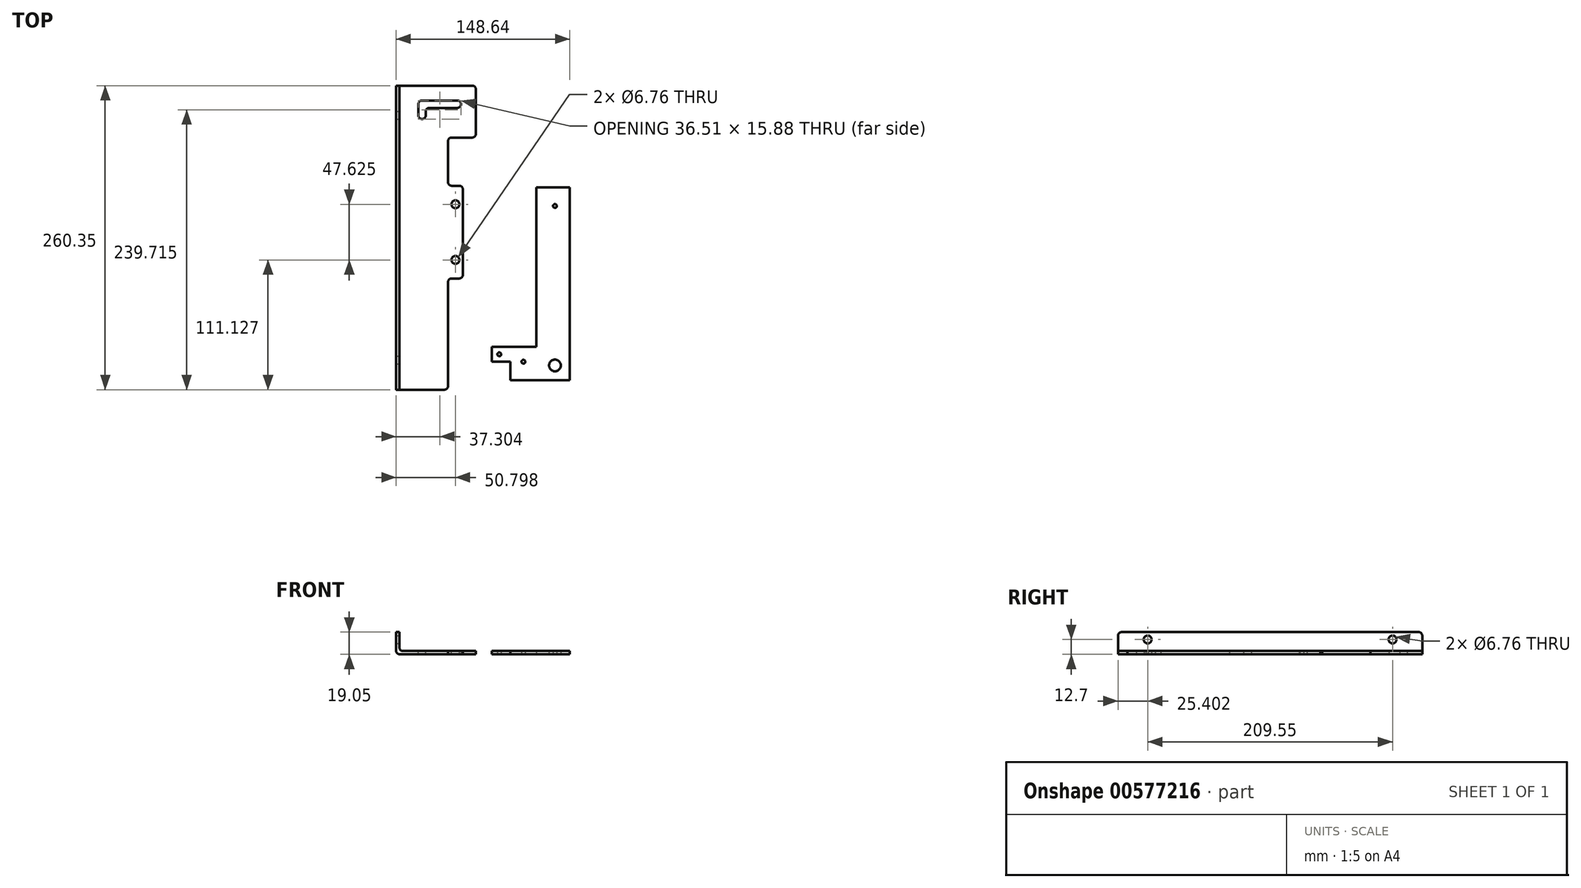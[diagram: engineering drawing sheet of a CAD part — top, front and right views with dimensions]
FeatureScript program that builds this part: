
annotation { "Feature Type Name" : "Feature", "Feature Type Description" : "" }
export const myFeature = defineFeature(function(context is Context, id is Id, definition is map)
    precondition{}
    {
        {
            var Q0;
            Q0=qCreatedBy(makeId("Top.planeOp"),FACE);
            var sketch = newSketch(context, id + "F0", { "sketchPlane" : qUnion([Q0])});
            skLineSegment(sketch, "E0", {"start": v(-43.32, 198.66) * mm, "end": v(-43.32, -61.69) * mm});
            skLineSegment(sketch, "E1", {"start": v(-43.32, -61.69) * mm, "end": v(1.13, -61.69) * mm});
            skLineSegment(sketch, "E2", {"start": v(1.13, -61.69) * mm, "end": v(1.13, 33.56) * mm});
            skLineSegment(sketch, "E3", {"start": v(1.13, 33.56) * mm, "end": v(13.83, 33.56) * mm});
            skLineSegment(sketch, "E4", {"start": v(13.83, 33.56) * mm, "end": v(13.83, 112.94) * mm});
            skLineSegment(sketch, "E5", {"start": v(13.83, 112.94) * mm, "end": v(1.13, 112.94) * mm});
            skLineSegment(sketch, "E6", {"start": v(1.13, 112.94) * mm, "end": v(1.13, 154.21) * mm});
            skLineSegment(sketch, "E7", {"start": v(1.13, 154.21) * mm, "end": v(24.94, 154.21) * mm});
            skLineSegment(sketch, "E8", {"start": v(24.94, 154.21) * mm, "end": v(24.94, 198.66) * mm});
            skLineSegment(sketch, "E9", {"start": v(-43.32, 198.66) * mm, "end": v(24.94, 198.66) * mm});
            skLineSegment(sketch, "E10", {"start": v(105.32, 111.48) * mm, "end": v(76.75, 111.48) * mm});
            skLineSegment(sketch, "E11", {"start": v(76.75, 111.48) * mm, "end": v(76.75, -25.05) * mm});
            skLineSegment(sketch, "E12", {"start": v(76.75, -25.05) * mm, "end": v(38.65, -25.05) * mm});
            skLineSegment(sketch, "E13", {"start": v(38.65, -25.05) * mm, "end": v(38.65, -37.75) * mm});
            skLineSegment(sketch, "E14", {"start": v(38.65, -37.75) * mm, "end": v(54.52, -37.75) * mm});
            skLineSegment(sketch, "E15", {"start": v(54.52, -37.75) * mm, "end": v(54.52, -53.62) * mm});
            skLineSegment(sketch, "E16", {"start": v(54.52, -53.62) * mm, "end": v(105.32, -53.62) * mm});
            skLineSegment(sketch, "E17", {"start": v(105.32, -53.62) * mm, "end": v(105.32, 111.48) * mm});
            skSolve(sketch);
        }
        {
            var Q0;
            Q0=makeQuery(id+"F0.imprint","IMPRINT",FACE,{"disambiguationData":[TD([[makeQuery(id+"F0.imprint","IMPRINT",EDGE,{"derivedFrom":sQuery(id+"F0.wireOp",EDGE,"E0")}),1.0]])]});
            extrude(context, id + "F1", {"entities" : qUnion([Q0]), "depth" : 19.05 * mm, "offsetDistance" : 25.4 * mm});
        }
        {
            var Q0;
            Q0=makeQuery(id+"F0.imprint","IMPRINT",FACE,{"disambiguationData":[TD([[makeQuery(id+"F0.imprint","IMPRINT",EDGE,{"derivedFrom":sQuery(id+"F0.wireOp",EDGE,"E10")}),1.0]])]});
            extrude(context, id + "F2", {"entities" : qUnion([Q0]), "depth" : 2.78 * mm, "offsetDistance" : 25.4 * mm});
        }
        {
            var Q0;
            Q0=makeQuery(id+"F1.opExtrude","CAP_FACE",FACE,{"disambiguationData":[OSD([sQuery(id+"F0.wireOp",EDGE,"E0"),sQuery(id+"F0.wireOp",EDGE,"E1"),sQuery(id+"F0.wireOp",EDGE,"E2"),sQuery(id+"F0.wireOp",EDGE,"E3"),sQuery(id+"F0.wireOp",EDGE,"E4"),sQuery(id+"F0.wireOp",EDGE,"E5"),sQuery(id+"F0.wireOp",EDGE,"E6"),sQuery(id+"F0.wireOp",EDGE,"E7"),sQuery(id+"F0.wireOp",EDGE,"E8"),sQuery(id+"F0.wireOp",EDGE,"E9")])],"isStart":false});
            var Q1;
            Q1=makeQuery(id+"F1.opExtrude","SWEPT_FACE",FACE,{"disambiguationData":[OSD([sQuery(id+"F0.wireOp",EDGE,"E4")])]});
            var Q2;
            Q2=makeQuery(id+"F1.opExtrude","SWEPT_FACE",FACE,{"disambiguationData":[OSD([sQuery(id+"F0.wireOp",EDGE,"E8")])]});
            var Q3;
            Q3=makeQuery(id+"F1.opExtrude","SWEPT_FACE",FACE,{"disambiguationData":[OSD([sQuery(id+"F0.wireOp",EDGE,"E1")])]});
            var Q4;
            Q4=makeQuery(id+"F1.opExtrude","SWEPT_FACE",FACE,{"disambiguationData":[OSD([sQuery(id+"F0.wireOp",EDGE,"E2")])]});
            var Q5;
            Q5=makeQuery(id+"F1.opExtrude","SWEPT_FACE",FACE,{"disambiguationData":[OSD([sQuery(id+"F0.wireOp",EDGE,"E3")])]});
            var Q6;
            Q6=makeQuery(id+"F1.opExtrude","SWEPT_FACE",FACE,{"disambiguationData":[OSD([sQuery(id+"F0.wireOp",EDGE,"E5")])]});
            var Q7;
            Q7=makeQuery(id+"F1.opExtrude","SWEPT_FACE",FACE,{"disambiguationData":[OSD([sQuery(id+"F0.wireOp",EDGE,"E6")])]});
            var Q8;
            Q8=makeQuery(id+"F1.opExtrude","SWEPT_FACE",FACE,{"disambiguationData":[OSD([sQuery(id+"F0.wireOp",EDGE,"E7")])]});
            var Q9;
            Q9=makeQuery(id+"F1.opExtrude","SWEPT_FACE",FACE,{"disambiguationData":[OSD([sQuery(id+"F0.wireOp",EDGE,"E9")])]});
            shell(context, id + "F3", {"entities" : qUnion([Q0, Q1, Q2, Q3, Q4, Q5, Q6, Q7, Q8, Q9]), "thickness" : 2.78 * mm});
        }
        {
            var Q0;
            Q0=makeQuery(id+"F3.opShell","OFFSET_FACE",FACE,{"disambiguationData":[OSD([sQuery(id+"F0.wireOp",EDGE,"E0"),sQuery(id+"F0.wireOp",EDGE,"E1"),sQuery(id+"F0.wireOp",EDGE,"E2"),sQuery(id+"F0.wireOp",EDGE,"E3"),sQuery(id+"F0.wireOp",EDGE,"E4"),sQuery(id+"F0.wireOp",EDGE,"E5"),sQuery(id+"F0.wireOp",EDGE,"E6"),sQuery(id+"F0.wireOp",EDGE,"E7"),sQuery(id+"F0.wireOp",EDGE,"E8"),sQuery(id+"F0.wireOp",EDGE,"E9")])]});
            var sketch = newSketch(context, id + "F4", { "sketchPlane" : qUnion([Q0])});
            skLineSegment(sketch, "E18", {"start": v(12.24, 185.96) * mm, "end": v(-24.27, 185.96) * mm});
            skLineSegment(sketch, "E19", {"start": v(-24.27, 185.96) * mm, "end": v(-24.27, 170.09) * mm});
            skLineSegment(sketch, "E20", {"start": v(-24.27, 170.09) * mm, "end": v(-17.92, 170.09) * mm});
            skLineSegment(sketch, "E21", {"start": v(-17.92, 170.09) * mm, "end": v(-17.92, 179.61) * mm});
            skLineSegment(sketch, "E22", {"start": v(-17.92, 179.61) * mm, "end": v(12.24, 179.61) * mm});
            skLineSegment(sketch, "E23", {"start": v(12.24, 179.61) * mm, "end": v(12.24, 185.96) * mm});
            skSolve(sketch);
        }
        {
            var Q0;
            Q0 = qSketchRegion(id + "F4", true);
            extrude(context, id + "F5", {"entities" : qUnion([Q0]), "operationType" : NewBodyOperationType.REMOVE, "oppositeDirection" : true, "depth" : 25.4 * mm, "offsetDistance" : 25.4 * mm});
        }
        {
            var Q0;
            Q0=makeQuery(id+"F3.opShell","OFFSET_FACE",FACE,{"disambiguationData":[OSD([sQuery(id+"F0.wireOp",EDGE,"E0"),sQuery(id+"F0.wireOp",EDGE,"E1"),sQuery(id+"F0.wireOp",EDGE,"E2"),sQuery(id+"F0.wireOp",EDGE,"E3"),sQuery(id+"F0.wireOp",EDGE,"E4"),sQuery(id+"F0.wireOp",EDGE,"E5"),sQuery(id+"F0.wireOp",EDGE,"E6"),sQuery(id+"F0.wireOp",EDGE,"E7"),sQuery(id+"F0.wireOp",EDGE,"E8"),sQuery(id+"F0.wireOp",EDGE,"E9")])]});
            var sketch = newSketch(context, id + "F6", { "sketchPlane" : qUnion([Q0])});
            skPoint(sketch, "E24", {"position": v(7.48, 97.06) * mm});
            skPoint(sketch, "E25", {"position": v(7.48, 49.44) * mm});
            skSolve(sketch);
        }
        {
            var Q0;
            Q0=sQuery(id+"F6.wireOp",VERTEX,"E24");
            var Q1;
            Q1=sQuery(id+"F6.wireOp",VERTEX,"E25");
            var Q2;
            Q2=makeQuery(id+"F1.opExtrude","SWEPT_BODY",BODY,{"disambiguationData":[OSD([sQuery(id+"F0.wireOp",EDGE,"E0"),sQuery(id+"F0.wireOp",EDGE,"E1"),sQuery(id+"F0.wireOp",EDGE,"E2"),sQuery(id+"F0.wireOp",EDGE,"E3"),sQuery(id+"F0.wireOp",EDGE,"E4"),sQuery(id+"F0.wireOp",EDGE,"E5"),sQuery(id+"F0.wireOp",EDGE,"E6"),sQuery(id+"F0.wireOp",EDGE,"E7"),sQuery(id+"F0.wireOp",EDGE,"E8"),sQuery(id+"F0.wireOp",EDGE,"E9")])]});
            hole(context, id + "F7", {"style" : HoleStyle.SIMPLE, "endStyle" : HoleEndStyle.BLIND, "standardTappedOrClearance" : lookupTablePath({ "standard" : "ANSI", "fit" : "Normal (ASME)", "size" : "1/4", "type" : "Clearance" }), "standardBlindInLast" : lookupTablePath({ "fit" : "Free", "standard" : "ANSI", "size" : "1/4", "type" : "Clearance" }), "holeDiameter" : 6.76 * mm, "holeDepth" : 12.7 * mm, "isTappedThrough" : true, "tappedDepth" : 12.7 * mm, "tapClearance" : 3, "locations" : qUnion([Q0, Q1]), "scope" : qUnion([Q2])});
        }
        {
            var Q0;
            Q0=makeQuery(id+"F0.imprint","IMPRINT",FACE,{"disambiguationData":[TD([[makeQuery(id+"F0.imprint","IMPRINT",EDGE,{"derivedFrom":sQuery(id+"F0.wireOp",EDGE,"E10")}),1.0]])]});
            var sketch = newSketch(context, id + "F8", { "sketchPlane" : qUnion([Q0])});
            skPoint(sketch, "E26", {"position": v(92.62, 95.6) * mm});
            skPoint(sketch, "E27", {"position": v(45, -31.4) * mm});
            skPoint(sketch, "E28", {"position": v(65.64, -37.75) * mm});
            skSolve(sketch);
        }
        {
            var Q0;
            Q0=sQuery(id+"F8.wireOp",VERTEX,"0d9547b9-0590-4271-b696-2fdcaec02221");
            var Q1;
            Q1=sQuery(id+"F8.wireOp",VERTEX,"E28");
            var Q2;
            Q2=sQuery(id+"F8.wireOp",VERTEX,"E27");
            var Q3;
            Q3=sQuery(id+"F8.wireOp",VERTEX,"E26");
            var Q4;
            Q4=makeQuery(id+"F2.opExtrude","SWEPT_BODY",BODY,{"disambiguationData":[OSD([sQuery(id+"F0.wireOp",EDGE,"E10"),sQuery(id+"F0.wireOp",EDGE,"E11"),sQuery(id+"F0.wireOp",EDGE,"E12"),sQuery(id+"F0.wireOp",EDGE,"E13"),sQuery(id+"F0.wireOp",EDGE,"E14"),sQuery(id+"F0.wireOp",EDGE,"E15"),sQuery(id+"F0.wireOp",EDGE,"E16"),sQuery(id+"F0.wireOp",EDGE,"E17")])]});
            hole(context, id + "F9", {"style" : HoleStyle.SIMPLE, "endStyle" : HoleEndStyle.BLIND, "oppositeDirection" : true, "standardTappedOrClearance" : lookupTablePath({ "standard" : "ANSI", "fit" : "Normal (ASME)", "size" : "#4", "type" : "Clearance" }), "standardBlindInLast" : lookupTablePath({ "fit" : "Free", "standard" : "ANSI", "size" : "#4", "type" : "Clearance" }), "holeDiameter" : 3.26 * mm, "holeDepth" : 12.7 * mm, "isTappedThrough" : true, "tappedDepth" : 12.7 * mm, "tapClearance" : 3, "locations" : qUnion([Q0, Q1, Q2, Q3]), "scope" : qUnion([Q4])});
        }
        {
            var Q0;
            Q0=makeQuery(id+"F0.imprint","IMPRINT",FACE,{"disambiguationData":[TD([[makeQuery(id+"F0.imprint","IMPRINT",EDGE,{"derivedFrom":sQuery(id+"F0.wireOp",EDGE,"E10")}),1.0]])]});
            var sketch = newSketch(context, id + "F10", { "sketchPlane" : qUnion([Q0])});
            skPoint(sketch, "E29", {"position": v(92.62, -40.92) * mm});
            skSolve(sketch);
        }
        {
            var Q0;
            Q0=makeQuery(id+"F3.opShell","OFFSET_FACE",FACE,{"disambiguationData":[OSD([sQuery(id+"F0.wireOp",EDGE,"E0")])]});
            var sketch = newSketch(context, id + "F11", { "sketchPlane" : qUnion([Q0])});
            skPoint(sketch, "E30", {"position": v(-36.29, 12.7) * mm});
            skPoint(sketch, "E31", {"position": v(173.26, 12.7) * mm});
            skSolve(sketch);
        }
        {
            var Q0;
            Q0=sQuery(id+"F11.wireOp",VERTEX,"E30");
            var Q1;
            Q1=sQuery(id+"F11.wireOp",VERTEX,"E31");
            var Q2;
            Q2=makeQuery(id+"F1.opExtrude","SWEPT_BODY",BODY,{"disambiguationData":[OSD([sQuery(id+"F0.wireOp",EDGE,"E0"),sQuery(id+"F0.wireOp",EDGE,"E1"),sQuery(id+"F0.wireOp",EDGE,"E2"),sQuery(id+"F0.wireOp",EDGE,"E3"),sQuery(id+"F0.wireOp",EDGE,"E4"),sQuery(id+"F0.wireOp",EDGE,"E5"),sQuery(id+"F0.wireOp",EDGE,"E6"),sQuery(id+"F0.wireOp",EDGE,"E7"),sQuery(id+"F0.wireOp",EDGE,"E8"),sQuery(id+"F0.wireOp",EDGE,"E9")])]});
            hole(context, id + "F12", {"style" : HoleStyle.SIMPLE, "endStyle" : HoleEndStyle.BLIND, "standardTappedOrClearance" : lookupTablePath({ "standard" : "ANSI", "fit" : "Normal (ASME)", "size" : "1/4", "type" : "Clearance" }), "standardBlindInLast" : lookupTablePath({ "fit" : "Free", "standard" : "ANSI", "size" : "1/4", "type" : "Clearance" }), "holeDiameter" : 6.76 * mm, "holeDepth" : 12.7 * mm, "isTappedThrough" : true, "tappedDepth" : 12.7 * mm, "tapClearance" : 3, "locations" : qUnion([Q0, Q1]), "scope" : qUnion([Q2])});
        }
        {
            var Q0;
            Q0=makeQuery(id+"F5.boolean.opBoolean","COPY",EDGE,{"derivedFrom":makeQuery(id+"F5.opExtrude","SWEPT_EDGE",EDGE,{"disambiguationData":[OSD([sQuery(id+"F4.wireOp",EDGE,"E19"),sQuery(id+"F4.wireOp",EDGE,"E20")])]})});
            var Q1;
            Q1=makeQuery(id+"F5.boolean.opBoolean","COPY",EDGE,{"derivedFrom":makeQuery(id+"F5.opExtrude","SWEPT_EDGE",EDGE,{"disambiguationData":[OSD([sQuery(id+"F4.wireOp",EDGE,"E18"),sQuery(id+"F4.wireOp",EDGE,"E19")])]})});
            var Q2;
            Q2=makeQuery(id+"F5.boolean.opBoolean","COPY",EDGE,{"derivedFrom":makeQuery(id+"F5.opExtrude","SWEPT_EDGE",EDGE,{"disambiguationData":[OSD([sQuery(id+"F4.wireOp",EDGE,"E20"),sQuery(id+"F4.wireOp",EDGE,"E21")])]})});
            var Q3;
            Q3=makeQuery(id+"F5.boolean.opBoolean","COPY",EDGE,{"derivedFrom":makeQuery(id+"F5.opExtrude","SWEPT_EDGE",EDGE,{"disambiguationData":[OSD([sQuery(id+"F4.wireOp",EDGE,"E21"),sQuery(id+"F4.wireOp",EDGE,"E22")])]})});
            var Q4;
            Q4=makeQuery(id+"F5.boolean.opBoolean","COPY",EDGE,{"derivedFrom":makeQuery(id+"F5.opExtrude","SWEPT_EDGE",EDGE,{"disambiguationData":[OSD([sQuery(id+"F4.wireOp",EDGE,"E18"),sQuery(id+"F4.wireOp",EDGE,"E23")])]})});
            var Q5;
            Q5=makeQuery(id+"F5.boolean.opBoolean","COPY",EDGE,{"derivedFrom":makeQuery(id+"F5.opExtrude","SWEPT_EDGE",EDGE,{"disambiguationData":[OSD([sQuery(id+"F4.wireOp",EDGE,"E22"),sQuery(id+"F4.wireOp",EDGE,"E23")])]})});
            var Q6;
            Q6=makeQuery(id+"F1.opExtrude","SWEPT_EDGE",EDGE,{"disambiguationData":[OSD([sQuery(id+"F0.wireOp",EDGE,"E8"),sQuery(id+"F0.wireOp",EDGE,"E9")])]});
            var Q7;
            Q7=makeQuery(id+"F1.opExtrude","SWEPT_EDGE",EDGE,{"disambiguationData":[OSD([sQuery(id+"F0.wireOp",EDGE,"E5"),sQuery(id+"F0.wireOp",EDGE,"E6")])]});
            var Q8;
            Q8=makeQuery(id+"F1.opExtrude","SWEPT_EDGE",EDGE,{"disambiguationData":[OSD([sQuery(id+"F0.wireOp",EDGE,"E6"),sQuery(id+"F0.wireOp",EDGE,"E7")])]});
            var Q9;
            Q9=makeQuery(id+"F1.opExtrude","SWEPT_EDGE",EDGE,{"disambiguationData":[OSD([sQuery(id+"F0.wireOp",EDGE,"E7"),sQuery(id+"F0.wireOp",EDGE,"E8")])]});
            var Q10;
            Q10=makeQuery(id+"F1.opExtrude","SWEPT_EDGE",EDGE,{"disambiguationData":[OSD([sQuery(id+"F0.wireOp",EDGE,"E4"),sQuery(id+"F0.wireOp",EDGE,"E5")])]});
            var Q11;
            Q11=makeQuery(id+"F1.opExtrude","SWEPT_EDGE",EDGE,{"disambiguationData":[OSD([sQuery(id+"F0.wireOp",EDGE,"E3"),sQuery(id+"F0.wireOp",EDGE,"E4")])]});
            var Q12;
            Q12=makeQuery(id+"F1.opExtrude","SWEPT_EDGE",EDGE,{"disambiguationData":[OSD([sQuery(id+"F0.wireOp",EDGE,"E2"),sQuery(id+"F0.wireOp",EDGE,"E3")])]});
            var Q13;
            Q13=makeQuery(id+"F1.opExtrude","SWEPT_EDGE",EDGE,{"disambiguationData":[OSD([sQuery(id+"F0.wireOp",EDGE,"E1"),sQuery(id+"F0.wireOp",EDGE,"E2")])]});
            var Q14;
            {var subQ0=sQuery(id+"F0.wireOp",EDGE,"E0");Q14=makeQuery(id+"F3.opShell","OFFSET_EDGE",EDGE,{"disambiguationData":[OSD([subQ0]),TDD([makeQuery(id+"F1.opExtrude","CAP_EDGE",EDGE,{"disambiguationData":[OSD([subQ0])],"isStart":true})])]});}
            var Q15;
            Q15=makeQuery(id+"F1.opExtrude","CAP_EDGE",EDGE,{"disambiguationData":[OSD([sQuery(id+"F0.wireOp",EDGE,"E1")])],"isStart":false});
            var Q16;
            Q16=makeQuery(id+"F1.opExtrude","CAP_EDGE",EDGE,{"disambiguationData":[OSD([sQuery(id+"F0.wireOp",EDGE,"E9")])],"isStart":false});
            var Q17;
            Q17=makeQuery(id+"F1.opExtrude","CAP_EDGE",EDGE,{"disambiguationData":[OSD([sQuery(id+"F0.wireOp",EDGE,"E0")])],"isStart":true});
            fillet(context, id + "F13", {"entities" : qUnion([Q0, Q1, Q2, Q3, Q4, Q5, Q6, Q7, Q8, Q9, Q10, Q11, Q12, Q13, Q14, Q15, Q16, Q17]), "radius" : 3.17 * mm, "tangentPropagation" : true, "allowEdgeOverflow" : false});
        }
        {
            var Q0;
            Q0=sQuery(id+"F10.wireOp",VERTEX,"E29");
            var Q1;
            Q1=makeQuery(id+"F2.opExtrude","SWEPT_BODY",BODY,{"disambiguationData":[OSD([sQuery(id+"F0.wireOp",EDGE,"E10"),sQuery(id+"F0.wireOp",EDGE,"E11"),sQuery(id+"F0.wireOp",EDGE,"E12"),sQuery(id+"F0.wireOp",EDGE,"E13"),sQuery(id+"F0.wireOp",EDGE,"E14"),sQuery(id+"F0.wireOp",EDGE,"E15"),sQuery(id+"F0.wireOp",EDGE,"E16"),sQuery(id+"F0.wireOp",EDGE,"E17")])]});
            hole(context, id + "F14", {"style" : HoleStyle.SIMPLE, "endStyle" : HoleEndStyle.BLIND, "oppositeDirection" : true, "standardTappedOrClearance" : lookupTablePath({ "standard" : "ANSI", "fit" : "Normal (ASME)", "size" : "3/8", "type" : "Clearance" }), "standardBlindInLast" : lookupTablePath({ "fit" : "Free", "standard" : "ANSI", "size" : "3/8", "type" : "Clearance" }), "holeDiameter" : 10.08 * mm, "holeDepth" : 12.7 * mm, "isTappedThrough" : true, "tappedDepth" : 12.7 * mm, "tapClearance" : 3, "locations" : qUnion([Q0]), "scope" : qUnion([Q1])});
        }
    });
